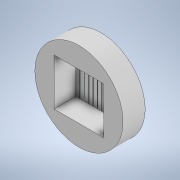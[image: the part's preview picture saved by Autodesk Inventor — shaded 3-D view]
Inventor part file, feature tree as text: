
AUTODESK INVENTOR PART (.ipt)
format: ipt  version: 2021 (Build 250183000, 183)  size: 447,488 bytes
history: native  units: in
note: dims shown in document units (in); Inventor stores cm internally (conversion verified against a paired STEP export)
features: sketch x5, extrude x5, projected_geometry x4, pattern_linear x2, plane x1, mirror x1
ambient origin geometry x8: Origin, YZ Plane, XZ Plane, XY Plane, X Axis, Y Axis, Z Axis, Center Point
bodies: Body1 (feature_tree)
feature tree (18):
  sketch  "Sketch1"  dims[d0=1.1295in d1=1.06in]
  plane  "Work Plane1"
  extrude  "Extrusion2"  Depth=1.06in
  extrude  "Extrusion3"  Depth=0.5in TaperAngle=0.0deg
  extrude  "Extrusion4"  Depth=0.085in
  pattern_linear  "Rectangular Pattern1"  Count1=12 Spacing1=0.1in
  extrude  "Extrusion5"  Depth=0.006in TaperAngle=0.0deg
  extrude  "Extrusion6"  Depth=0.2in
  pattern_linear  "Rectangular Pattern2"  Spacing1=0.0in  [1 undecoded]
  mirror  "Mirror1"
  sketch  "Sketch2"  dims[d4=2.0in d5=0.5in d6=0.0in]
  sketch  "Sketch3"  dims[d7=0.25in d8=0.0in d9=0.085in]
  projected_geometry  "Projected Loop1"
  projected_geometry  "Projected Loop2"
  sketch  "Sketch4"  dims[d10=0.006in d11=0.0in d12=4.7244in d14=0.1in]
  projected_geometry  "Projected Loop3"
  sketch  "Sketch5"  dims[d15=0.01in d16=0.006in d17=0.0in d18=0.0394in d20=0.0in d21=0.0in d22=2.3622in d24=0.2in]
  projected_geometry  "Projected Loop4"
note: 1 required parameter value undecoded (feature->parameter linkage not recoverable at this tier; creation-order binding heuristic only, values carry confidence <= 0.55)
